# Revit family: CMH-WM500V-A
name_source: partatom
category: Mechanical Equipment
revit_build: Autodesk Revit 2016 (Build: 20150220_1215(x64)
units: mm (PartAtom-declared; Revit-internal decimal feet)

## family parameters
Always vertical = Yes
Cut with Voids When Loaded = No
OmniClass Number = 23.75.00.00
OmniClass Title = Climate Control (HVAC)
Part Type = Normal
Room Calculation Point = No
Round Connector Dimension = Use Radius
Shared = No
Work Plane-Based = No

## types (24) — shared parameters
Applicable temperature range of installation site = -5 to 52
Connectable Outdoor/Heat source Unit = PUHY-M400 to 500YNW-A1(-BS)/PUHY-EM400 to 500YNW-A1(-BS)
Cooling Power Input (kW) = 1.06
Depth = 740 mm  [stored 2.42782 ft]
Description = Hydro unit
External Finish = Pre-coated galvanized steel sheets
Gas pipe_radius = 14.29 mm  [stored 0.0468832 ft]
Heating Power Input (kW) = 1.06
Height = 660 mm
Manufacturer = Mitsubishi Electric Corporation
Model = CMH-WM500V-A
Phase = 1
Sound Pressure Level (dB(A)) = 60
Space View = Yes
Subcategory = HVAC
URL = http://www.mitsubishielectric.com
Unit Weight (kg) = 152
Water Pipe radius (EXP. Vessel) = 11 mm  [stored 0.0360892 ft]
Water Pipe radius (From Indoor Unit) = 25 mm  [stored 0.082021 ft]
Water Pipe radius (Inlet) = 11 mm  [stored 0.0360892 ft]
Water Pipe radius (To Indoor Unit) = 25 mm  [stored 0.082021 ft]
Width = 920 mm  [stored 3.01837 ft]
zero-valued in all types: Equip_No., SerialNumber, TagNumber

## per-type parameters (varying)
| type | Cooling Current (A) | Heating Current (A) | Hertz | Liquid pipe_radius | Voltage |
| CMH-WM500V-A_220V_50Hz_To M400 | 5.47 | 5.47 | 50 Hz | 6.35 mm  [stored 0.0208333 ft] | 220 V |
| CMH-WM500V-A_220V_60Hz_To M400 | 5.47 | 5.47 | 60 Hz | 6.35 mm  [stored 0.0208333 ft] | 220 V |
| CMH-WM500V-A_230V_50Hz_To M400 | 5.23 | 5.23 | 50 Hz | 6.35 mm  [stored 0.0208333 ft] | 230 V |
| CMH-WM500V-A_230V_60Hz_To M400 | 5.23 | 5.23 | 60 Hz | 6.35 mm  [stored 0.0208333 ft] | 230 V |
| CMH-WM500V-A_240V_50Hz_To M400 | 5.02 | 5.02 | 50 Hz | 6.35 mm  [stored 0.0208333 ft] | 240 V |
| CMH-WM500V-A_240V_60Hz_To M400 | 5.02 | 5.02 | 60 Hz | 6.35 mm  [stored 0.0208333 ft] | 240 V |
| CMH-WM500V-A_220V_50Hz_To M450/500 | 5.47 | 5.47 | 50 Hz | 7.94 mm  [stored 0.0260499 ft] | 220 V |
| CMH-WM500V-A_220V_60Hz_To M450/500 | 5.47 | 5.47 | 60 Hz | 7.94 mm  [stored 0.0260499 ft] | 220 V |
| CMH-WM500V-A_230V_50Hz_To M450/500 | 5.23 | 5.23 | 50 Hz | 7.94 mm  [stored 0.0260499 ft] | 230 V |
| CMH-WM500V-A_230V_60Hz_To M450/500 | 5.23 | 5.23 | 60 Hz | 7.94 mm  [stored 0.0260499 ft] | 230 V |
| CMH-WM500V-A_240V_50Hz_To M450/500 | 5.02 | 5.02 | 50 Hz | 7.94 mm  [stored 0.0260499 ft] | 240 V |
| CMH-WM500V-A_240V_60Hz_To M450/500 | 5.02 | 5.02 | 60 Hz | 7.94 mm  [stored 0.0260499 ft] | 240 V |
| CMH-WM500V-A_220V_50Hz_To EM400 | 5.47 | 5.47 | 50 Hz | 6.35 mm  [stored 0.0208333 ft] | 220 V |
| CMH-WM500V-A_220V_60Hz_To EM400 | 5.47 | 5.47 | 60 Hz | 6.35 mm  [stored 0.0208333 ft] | 220 V |
| CMH-WM500V-A_230V_50Hz_To EM400 | 5.23 | 5.23 | 50 Hz | 6.35 mm  [stored 0.0208333 ft] | 230 V |
| CMH-WM500V-A_230V_60Hz_To EM400 | 5.23 | 5.23 | 60 Hz | 6.35 mm  [stored 0.0208333 ft] | 230 V |
| CMH-WM500V-A_240V_50Hz_To EM400 | 5.02 | 5.02 | 50 Hz | 6.35 mm  [stored 0.0208333 ft] | 240 V |
| CMH-WM500V-A_240V_60Hz_To EM400 | 5.02 | 5.02 | 60 Hz | 6.35 mm  [stored 0.0208333 ft] | 240 V |
| CMH-WM500V-A_220V_50Hz_To EM450/500 | 5.47 | 5.47 | 50 Hz | 7.94 mm  [stored 0.0260499 ft] | 220 V |
| CMH-WM500V-A_220V_60Hz_To EM450/500 | 5.47 | 5.47 | 60 Hz | 7.94 mm  [stored 0.0260499 ft] | 220 V |
| CMH-WM500V-A_230V_50Hz_To EM450/500 | 5.23 | 5.23 | 50 Hz | 7.94 mm  [stored 0.0260499 ft] | 230 V |
| CMH-WM500V-A_230V_60Hz_To EM450/500 | 5.23 | 5.23 | 60 Hz | 7.94 mm  [stored 0.0260499 ft] | 230 V |
| CMH-WM500V-A_240V_50Hz_To EM450/500 | 5.02 | 5.02 | 50 Hz | 7.94 mm  [stored 0.0260499 ft] | 240 V |
| CMH-WM500V-A_240V_60Hz_To EM450/500 | 5.02 | 5.02 | 60 Hz | 7.94 mm  [stored 0.0260499 ft] | 240 V |

note: [stored X ft] marks values corroborated as IEEE doubles in the binary element streams (Revit-internal decimal feet)

## geometry (parser evidence)
native form markers: Blend x40, Sweep x1
no freeform markers — native parametric forms only
